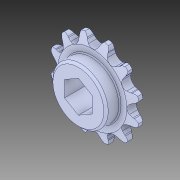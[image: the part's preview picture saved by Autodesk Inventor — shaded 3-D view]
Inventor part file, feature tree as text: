
AUTODESK INVENTOR PART (.ipt)
format: ipt  version: 2019 (Build 230136000, 136)  size: 356,864 bytes
history: native  units: in
note: dims shown in document units (in); Inventor stores cm internally (conversion verified against a paired STEP export)
features: chamfer x1
ambient origin geometry x8: Origin, YZ Plane, XZ Plane, XY Plane, X Axis, Y Axis, Z Axis, Center Point
bodies: Solid1 (feature_tree)
feature tree (1):
  chamfer  "Chamfer1"  [1 undecoded]
note: 1 required parameter value undecoded (feature->parameter linkage not recoverable at this tier; creation-order binding heuristic only, values carry confidence <= 0.55)
